# Revit family: 873-00-002-DN450-600
name_source: partatom
category: Pipe Accessories
units: mm (PartAtom-declared; Revit-internal decimal feet)

## family parameters
Always vertical = Yes
Cut with Voids When Loaded = No
Part Type = Valve - Breaks Into
Round Connector Dimension = Use Diameter
Shared = No
Work Plane-Based = No

## types (3) — shared parameters
873-0450-00-741000 = DN450_PN25
873-0500-00-741000 = DN500_PN25
873-0600-00-741000 = DN600_PN25
Angle = 22.50°
Body_Wallthicknss = 10 mm  [stored 0.0328084 ft]
Description_ = AVK DISMANTLING JOINT
Flange_thickness = 20 mm  [stored 0.0656168 ft]
Search_table = 873-00-002-DN450-600
URL product pages = https://www.avkvalves.com

## per-type parameters (varying)
| type | A | DN | Id(Radius) | L | T | d1 | d2 |
| DN450 | 255 mm  [stored 0.836614 ft] | 450 mm  [stored 1.47638 ft] | 225 mm  [stored 0.738189 ft] | 500 mm  [stored 1.64042 ft] | 33 mm  [stored 0.108268 ft] | 600 mm  [stored 1.9685 ft] | 335 mm  [stored 1.09908 ft] |
| DN500 | 275 mm  [stored 0.902231 ft] | 500 mm  [stored 1.64042 ft] | 250 mm  [stored 0.82021 ft] | 500 mm  [stored 1.64042 ft] | 33 mm  [stored 0.108268 ft] | 660 mm  [stored 2.16535 ft] | 365 mm  [stored 1.19751 ft] |
| DN600 | 295 mm  [stored 0.967848 ft] | 600 mm  [stored 1.9685 ft] | 300 mm  [stored 0.984252 ft] | 550 mm  [stored 1.80446 ft] | 36 mm  [stored 0.11811 ft] | 770 mm  [stored 2.52625 ft] | 423 mm |

note: [stored X ft] marks values corroborated as IEEE doubles in the binary element streams (Revit-internal decimal feet)

## geometry (parser evidence)
native form markers: Sweep x7
no freeform markers — native parametric forms only
